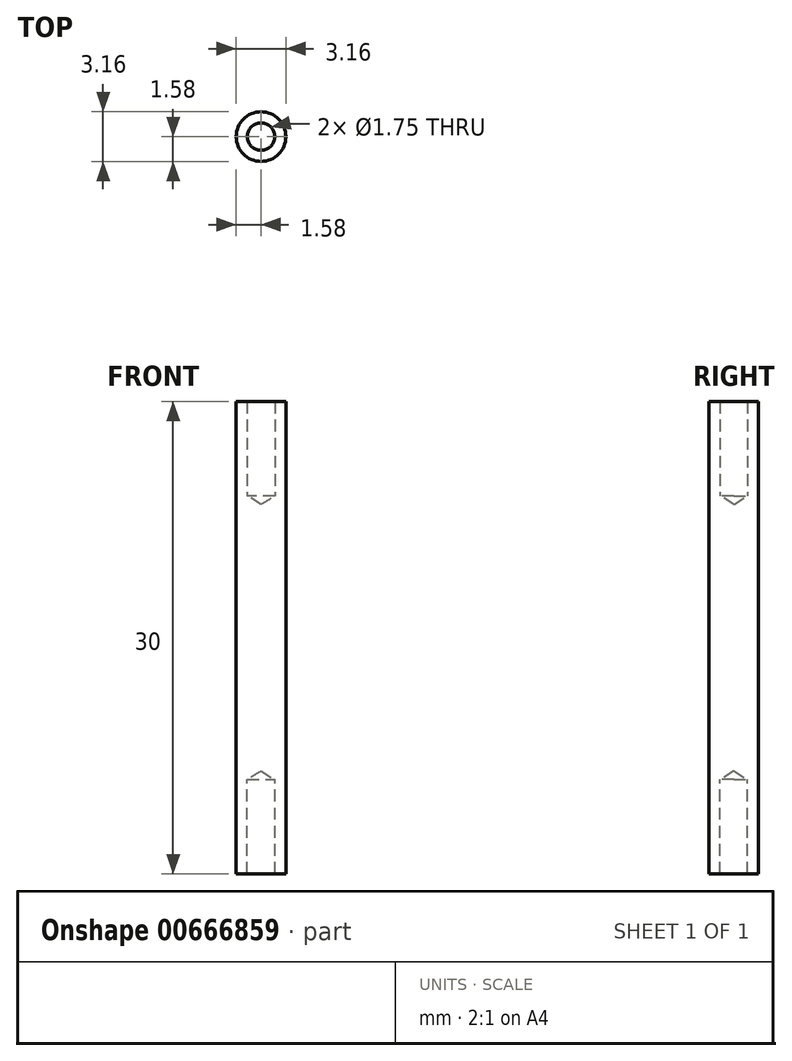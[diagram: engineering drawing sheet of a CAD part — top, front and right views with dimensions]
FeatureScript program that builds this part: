
annotation { "Feature Type Name" : "Feature", "Feature Type Description" : "" }
export const myFeature = defineFeature(function(context is Context, id is Id, definition is map)
    precondition{}
    {
        {
            var Q0;
            Q0=qCreatedBy(makeId("Top.planeOp"),FACE);
            var sketch = newSketch(context, id + "F0", { "sketchPlane" : qUnion([Q0])});
            skCircle(sketch, "E0", {"center": v(0, 0) * mm, "radius": 1.57 * mm});
            skSolve(sketch);
        }
        {
            var Q0;
            Q0 = qSketchRegion(id + "F0", true);
            extrude(context, id + "F1", {"entities" : qUnion([Q0]), "depth" : 30 * mm, "offsetDistance" : 25 * mm});
        }
        {
            var Q0;
            Q0=makeQuery(id+"F1.opExtrude","CAP_FACE",FACE,{"disambiguationData":[OSD([sQuery(id+"F0.wireOp",EDGE,"ikXEF6NJ-NwL5-w3BU-QjmC-NVrDih6iadRm"),sQuery(id+"F0.wireOp",EDGE,"E0")])],"isStart":false});
            var sketch = newSketch(context, id + "F2", { "sketchPlane" : qUnion([Q0])});
            skPoint(sketch, "E1", {"position": v(0, 0) * mm});
            skSolve(sketch);
        }
        {
            var Q0;
            Q0=sQuery(id+"F2.wireOp",VERTEX,"E1");
            var Q1;
            Q1=makeQuery(id+"F1.opExtrude","SWEPT_BODY",BODY,{"disambiguationData":[OSD([sQuery(id+"F0.wireOp",EDGE,"E0")])]});
            hole(context, id + "F3", {"style" : HoleStyle.SIMPLE, "endStyle" : HoleEndStyle.BLIND, "standardTappedOrClearance" : lookupTablePath({ "standard" : "ISO", "engagement" : "75%", "pitch" : "0.25 mm", "size" : "M2", "type" : "Tapped" }), "standardBlindInLast" : lookupTablePath({ "standard" : "ISO", "fit" : "Normal", "engagement" : "75%", "pitch" : "0.25 mm", "size" : "M2", "type" : "Clearance & tapped" }), "holeDiameter" : 1.75 * mm, "majorDiameter" : 2 * mm, "showTappedDepth" : true, "holeDepth" : 6 * mm, "isTappedThrough" : true, "tappedDepth" : 5.25 * mm, "tapClearance" : 3, "locations" : qUnion([Q0]), "scope" : qUnion([Q1])});
        }
        {
            var Q0;
            Q0=makeQuery(id+"F1.opExtrude","CAP_FACE",FACE,{"disambiguationData":[OSD([sQuery(id+"F0.wireOp",EDGE,"E0")])],"isStart":true});
            var sketch = newSketch(context, id + "F4", { "sketchPlane" : qUnion([Q0])});
            skPoint(sketch, "E2", {"position": v(0, 0) * mm});
            skSolve(sketch);
        }
        {
            var Q0;
            Q0=sQuery(id+"F4.wireOp",VERTEX,"E2");
            var Q1;
            Q1=makeQuery(id+"F1.opExtrude","SWEPT_BODY",BODY,{"disambiguationData":[OSD([sQuery(id+"F0.wireOp",EDGE,"E0")])]});
            hole(context, id + "F5", {"style" : HoleStyle.SIMPLE, "endStyle" : HoleEndStyle.BLIND, "standardTappedOrClearance" : lookupTablePath({ "standard" : "ISO", "engagement" : "75%", "pitch" : "0.25 mm", "size" : "M2", "type" : "Tapped" }), "standardBlindInLast" : lookupTablePath({ "fit" : "Normal", "standard" : "ISO", "engagement" : "75%", "pitch" : "0.25 mm", "size" : "M2", "type" : "Clearance & tapped" }), "holeDiameter" : 1.75 * mm, "majorDiameter" : 2 * mm, "showTappedDepth" : true, "holeDepth" : 6 * mm, "isTappedThrough" : true, "tappedDepth" : 5.25 * mm, "tapClearance" : 3, "locations" : qUnion([Q0]), "scope" : qUnion([Q1])});
        }
    });
